# Revit family: Lighting-Linear-Acclaim-Aqua Graze
name_source: partatom
category: Lighting Fixtures
revit_build: Autodesk Revit 2016 (Build: 20170117_1200(x64)
units: mm (PartAtom-declared; Revit-internal decimal feet)

## family parameters
Cut with Voids When Loaded = No
Host = Face
Light Source = Yes
Part Type = Normal
Room Calculation Point = No
Round Connector Dimension = Use Diameter
Shared = No

## types (2) — shared parameters
Apparent Load = 0 VA
Color Filter = 16777215
Default Elevation = 4' - 0"
Description = Graze Lighting
Dimming Lamp Color Temperature Shift = <None>
Housing Finish = Aluminum
Lamp = LED
Manufacturer = Acclaim Lighting
Number of Poles = 1
Photometric Web File = generic
Power Factor = 1
Tilt Angle = -90.00°
URL = http://www.acclaimlighting.com
Voltage = 0 V

## per-type parameters (varying)
| type | Emit from Line Length | Length | Model |
| A | 1' - 0" | 1' - 0" | Dyna Graze Exterior HO |
| D | 4' - 0" | 4' - 0" | Aqua Graze |

## geometry (parser evidence)
native form markers: Blend x13, Sweep x2
no freeform markers — native parametric forms only
